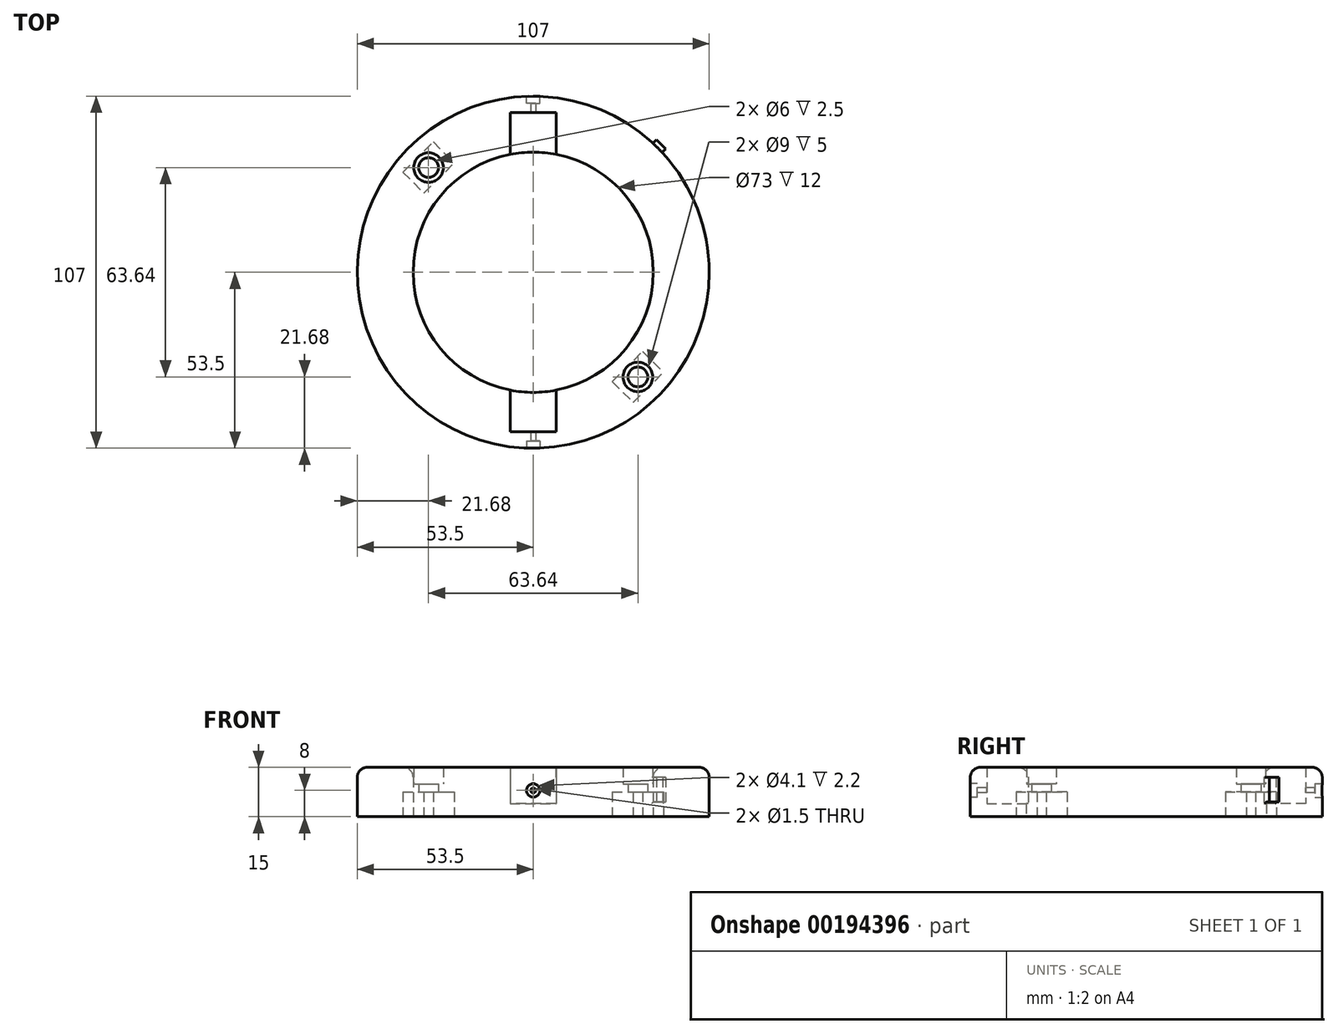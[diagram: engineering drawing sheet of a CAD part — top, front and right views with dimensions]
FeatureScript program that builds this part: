
annotation { "Feature Type Name" : "Feature", "Feature Type Description" : "" }
export const myFeature = defineFeature(function(context is Context, id is Id, definition is map)
    precondition{}
    {
        {
            var Q0;
            Q0=qCreatedBy(makeId("Top.planeOp"),FACE);
            var sketch = newSketch(context, id + "F0", { "sketchPlane" : qUnion([Q0])});
            skCircle(sketch, "E0", {"center": v(0, 0) * mm, "radius": 36.5 * mm});
            skCircle(sketch, "E1", {"center": v(0, 0) * mm, "radius": 53.5 * mm});
            skSolve(sketch);
        }
        {
            var Q0;
            Q0=makeQuery(id+"F0.imprint","IMPRINT",FACE,{"disambiguationData":[TD([[makeQuery(id+"F0.imprint","IMPRINT",EDGE,{"derivedFrom":sQuery(id+"F0.wireOp",EDGE,"E0")}),-1.0]])]});
            extrude(context, id + "F1", {"entities" : qUnion([Q0]), "depth" : 15 * mm});
        }
        {
            var Q0;
            Q0=qCreatedBy(makeId("Top.planeOp"),FACE);
            var sketch = newSketch(context, id + "F2", { "sketchPlane" : qUnion([Q0])});
            skPoint(sketch, "E2", {"position": v(0, 36.5) * mm});
            skPoint(sketch, "E3", {"position": v(0, -33.5) * mm});
            skPoint(sketch, "E4", {"position": v(0, 33.5) * mm});
            skPoint(sketch, "E5", {"position": v(0, 50.5) * mm});
            skPoint(sketch, "E6", {"position": v(0, -36.5) * mm});
            skPoint(sketch, "E7", {"position": v(0, -50.5) * mm});
            skPoint(sketch, "E8", {"position": v(0, 53.5) * mm});
            skPoint(sketch, "E9", {"position": v(0, -53.5) * mm});
            skLineSegment(sketch, "E10", {"start": v(25.8, -25.8) * mm, "end": v(-25.8, 25.8) * mm});
            skLineSegment(sketch, "E11", {"start": v(-25.8, -25.8) * mm, "end": v(25.8, 25.8) * mm});
            skLineSegment(sketch, "E12", {"start": v(-5, 53.5) * mm, "end": v(5, -53.5) * mm});
            skLineSegment(sketch, "E13", {"start": v(0, 53.5) * mm, "end": v(-5, 53.5) * mm});
            skLineSegment(sketch, "E14", {"start": v(0, -53.5) * mm, "end": v(5, -53.5) * mm});
            skSolve(sketch);
        }
        {
            var Q0;
            Q0=sQuery(id+"F2.wireOp",EDGE,"E10");
            cPlane(context, id + "F3", {"entities" : qUnion([Q0]), "cplaneType" : CPlaneType.LINE_ANGLE, "offset" : 25 * mm, "angle" : 90 * degree, "width" : 150 * mm, "height" : 150 * mm});
        }
        {
            var Q0;
            Q0=makeQuery(id+"F1.opExtrude","CAP_FACE",FACE,{"disambiguationData":[OSD([sQuery(id+"F0.wireOp",EDGE,"E0"),sQuery(id+"F0.wireOp",EDGE,"E1")])],"isStart":false});
            var sketch = newSketch(context, id + "F4", { "sketchPlane" : qUnion([Q0])});
            skPoint(sketch, "E15", {"position": v(-31.82, 31.82) * mm});
            skPoint(sketch, "E16", {"position": v(31.82, -31.82) * mm});
            skSolve(sketch);
        }
        {
            var Q0;
            Q0=sQuery(id+"F4.wireOp",VERTEX,"E15");
            var Q1;
            Q1=sQuery(id+"F4.wireOp",VERTEX,"E16");
            var Q2;
            Q2=makeQuery(id+"F1.opExtrude","SWEPT_BODY",BODY,{"disambiguationData":[OSD([sQuery(id+"F0.wireOp",EDGE,"E0"),sQuery(id+"F0.wireOp",EDGE,"E1")])]});
            hole(context, id + "F5", {"style" : HoleStyle.C_BORE, "endStyle" : HoleEndStyle.THROUGH, "holeDiameter" : 6 * mm, "cBoreDiameter" : 9 * mm, "cBoreDepth" : 5 * mm, "locations" : qUnion([Q0, Q1]), "scope" : qUnion([Q2]), "isTappedThrough" : true});
        }
        {
            var Q0;
            Q0=qCreatedBy(makeId("Front.planeOp"),FACE);
            var Q1;
            Q1=sQuery(id+"F2.wireOp",VERTEX,"E4");
            cPlane(context, id + "F6", {"entities" : qUnion([Q0, Q1]), "cplaneType" : CPlaneType.PLANE_POINT, "offset" : 25 * mm, "width" : 150 * mm, "height" : 150 * mm});
        }
        {
            var Q0;
            Q0=qCreatedBy(id+"F6.planeOp",FACE);
            var sketch = newSketch(context, id + "F7", { "sketchPlane" : qUnion([Q0])});
            skLineSegment(sketch, "E17.bottom", {"start": v(-7, 15) * mm, "end": v(7, 15) * mm});
            skLineSegment(sketch, "E17.top", {"start": v(-7, 4) * mm, "end": v(7, 4) * mm});
            skLineSegment(sketch, "E17.left", {"start": v(-7, 15) * mm, "end": v(-7, 4) * mm});
            skLineSegment(sketch, "E17.right", {"start": v(7, 15) * mm, "end": v(7, 4) * mm});
            skSolve(sketch);
        }
        {
            var Q0;
            Q0=makeQuery(id+"F7.imprint","IMPRINT",FACE,{"disambiguationData":[TD([[makeQuery(id+"F7.imprint","IMPRINT",EDGE,{"derivedFrom":sQuery(id+"F7.wireOp",EDGE,"E17.bottom")}),-1.0]])]});
            extrude(context, id + "F8", {"entities" : qUnion([Q0]), "operationType" : NewBodyOperationType.REMOVE, "oppositeDirection" : true, "depth" : 15 * mm});
        }
        {
            var Q0;
            Q0=qCreatedBy(makeId("Front.planeOp"),FACE);
            var Q1;
            Q1=sQuery(id+"F2.wireOp",VERTEX,"E3");
            cPlane(context, id + "F9", {"entities" : qUnion([Q0, Q1]), "cplaneType" : CPlaneType.PLANE_POINT, "offset" : 25 * mm, "width" : 150 * mm, "height" : 150 * mm});
        }
        {
            var Q0;
            Q0=qCreatedBy(id+"F9.planeOp",FACE);
            var sketch = newSketch(context, id + "F10", { "sketchPlane" : qUnion([Q0])});
            skLineSegment(sketch, "E18.bottom", {"start": v(7, 15) * mm, "end": v(-7, 15) * mm});
            skLineSegment(sketch, "E18.top", {"start": v(7, 4) * mm, "end": v(-7, 4) * mm});
            skLineSegment(sketch, "E18.left", {"start": v(7, 15) * mm, "end": v(7, 4) * mm});
            skLineSegment(sketch, "E18.right", {"start": v(-7, 15) * mm, "end": v(-7, 4) * mm});
            skSolve(sketch);
        }
        {
            var Q0;
            Q0=makeQuery(id+"F10.imprint","IMPRINT",FACE,{"disambiguationData":[TD([[makeQuery(id+"F10.imprint","IMPRINT",EDGE,{"derivedFrom":sQuery(id+"F10.wireOp",EDGE,"E18.bottom")}),1.0]])]});
            extrude(context, id + "F11", {"entities" : qUnion([Q0]), "operationType" : NewBodyOperationType.REMOVE, "depth" : 15 * mm});
        }
        {
            var Q0;
            Q0=qCreatedBy(makeId("Front.planeOp"),FACE);
            var Q1;
            Q1=sQuery(id+"F2.wireOp",VERTEX,"E9");
            cPlane(context, id + "F12", {"entities" : qUnion([Q0, Q1]), "cplaneType" : CPlaneType.PLANE_POINT, "offset" : 25 * mm, "width" : 150 * mm, "height" : 150 * mm});
        }
        {
            var Q0;
            Q0=qCreatedBy(id+"F12.planeOp",FACE);
            var sketch = newSketch(context, id + "F13", { "sketchPlane" : qUnion([Q0])});
            skCircle(sketch, "E19", {"center": v(0, 8) * mm, "radius": 2.05 * mm});
            skSolve(sketch);
        }
        {
            var Q0;
            Q0=makeQuery(id+"F13.imprint","IMPRINT",FACE,{"disambiguationData":[TD([[makeQuery(id+"F13.imprint","IMPRINT",EDGE,{"derivedFrom":sQuery(id+"F13.wireOp",EDGE,"E19")}),1.0]])]});
            extrude(context, id + "F14", {"entities" : qUnion([Q0]), "operationType" : NewBodyOperationType.REMOVE, "oppositeDirection" : true, "depth" : 2.2 * mm});
        }
        {
            var Q0;
            Q0=qCreatedBy(makeId("Front.planeOp"),FACE);
            var Q1;
            Q1=sQuery(id+"F2.wireOp",VERTEX,"E8");
            cPlane(context, id + "F15", {"entities" : qUnion([Q0, Q1]), "cplaneType" : CPlaneType.PLANE_POINT, "offset" : 25 * mm, "width" : 150 * mm, "height" : 150 * mm});
        }
        {
            var Q0;
            Q0=qCreatedBy(id+"F15.planeOp",FACE);
            var sketch = newSketch(context, id + "F16", { "sketchPlane" : qUnion([Q0])});
            skCircle(sketch, "E20", {"center": v(0, 8) * mm, "radius": 2.05 * mm});
            skSolve(sketch);
        }
        {
            var Q0;
            Q0=makeQuery(id+"F16.imprint","IMPRINT",FACE,{"disambiguationData":[TD([[makeQuery(id+"F16.imprint","IMPRINT",EDGE,{"derivedFrom":sQuery(id+"F16.wireOp",EDGE,"E20")}),1.0]])]});
            extrude(context, id + "F17", {"entities" : qUnion([Q0]), "operationType" : NewBodyOperationType.REMOVE, "depth" : 2.2 * mm});
        }
        {
            var Q0;
            Q0=makeQuery(id+"F1.opExtrude","CAP_FACE",FACE,{"disambiguationData":[OSD([sQuery(id+"F0.wireOp",EDGE,"E0"),sQuery(id+"F0.wireOp",EDGE,"E1")])],"isStart":true});
            var sketch = newSketch(context, id + "F18", { "sketchPlane" : qUnion([Q0])});
            skLineSegment(sketch, "E21.bottom", {"start": v(-39.6, -30.4) * mm, "end": v(-33.23, -24.04) * mm});
            skLineSegment(sketch, "E21.top", {"start": v(-30.4, -39.6) * mm, "end": v(-24.04, -33.23) * mm});
            skLineSegment(sketch, "E21.left", {"start": v(-39.6, -30.4) * mm, "end": v(-30.4, -39.6) * mm});
            skLineSegment(sketch, "E21.right", {"start": v(-33.23, -24.04) * mm, "end": v(-24.04, -33.23) * mm});
            skLineSegment(sketch, "E22.bottom", {"start": v(24.04, 33.23) * mm, "end": v(30.4, 39.6) * mm});
            skLineSegment(sketch, "E22.top", {"start": v(33.23, 24.04) * mm, "end": v(39.6, 30.4) * mm});
            skLineSegment(sketch, "E22.left", {"start": v(24.04, 33.23) * mm, "end": v(33.23, 24.04) * mm});
            skLineSegment(sketch, "E22.right", {"start": v(30.4, 39.6) * mm, "end": v(39.6, 30.4) * mm});
            skSolve(sketch);
        }
        {
            var Q0;
            Q0=makeQuery(id+"F18.imprint","IMPRINT",FACE,{"disambiguationData":[TD([[makeQuery(id+"F18.imprint","IMPRINT",EDGE,{"derivedFrom":sQuery(id+"F18.wireOp",EDGE,"E21.bottom")}),-1.0]])]});
            extrude(context, id + "F19", {"entities" : qUnion([Q0]), "operationType" : NewBodyOperationType.REMOVE, "oppositeDirection" : true, "depth" : 7.5 * mm});
        }
        {
            var Q0;
            Q0 = qSketchRegion(id + "F18", true);
            extrude(context, id + "F20", {"entities" : qUnion([Q0]), "operationType" : NewBodyOperationType.REMOVE, "oppositeDirection" : true, "depth" : 7.5 * mm});
        }
        {
            var Q0;
            Q0=makeQuery(id+"F1.opExtrude","CAP_EDGE",EDGE,{"disambiguationData":[OSD([sQuery(id+"F0.wireOp",EDGE,"E0")])],"isStart":false});
            fillet(context, id + "F21", {"entities" : qUnion([Q0]), "radius" : 3 * mm, "tangentPropagation" : true, "allowEdgeOverflow" : false});
        }
        {
            var Q0;
            Q0=makeQuery(id+"F1.opExtrude","CAP_EDGE",EDGE,{"disambiguationData":[OSD([sQuery(id+"F0.wireOp",EDGE,"E1")])],"isStart":false});
            fillet(context, id + "F22", {"entities" : qUnion([Q0]), "radius" : 3 * mm, "tangentPropagation" : true, "allowEdgeOverflow" : false});
        }
        {
            var Q0;
            Q0=qCreatedBy(makeId("Top.planeOp"),FACE);
            var sketch = newSketch(context, id + "F23", { "sketchPlane" : qUnion([Q0])});
            skPoint(sketch, "E23", {"position": v(-37.83, 37.83) * mm});
            skPoint(sketch, "E24.1.0", {"position": v(-37.83, -37.83) * mm});
            skPoint(sketch, "E24.2.0", {"position": v(37.83, -37.83) * mm});
            skPoint(sketch, "E24.3.0", {"position": v(37.83, 37.83) * mm});
            skPoint(sketch, "E24.center", {"position": v(0, 0) * mm});
            skLineSegment(sketch, "E25", {"start": v(37.83, 37.83) * mm, "end": v(74.08, 1.58) * mm});
            skLineSegment(sketch, "E26", {"start": v(37.83, -37.83) * mm, "end": v(13.7, -61.95) * mm});
            skLineSegment(sketch, "E27", {"start": v(-37.83, -37.83) * mm, "end": v(-65, -10.65) * mm});
            skLineSegment(sketch, "E28", {"start": v(-37.83, 37.83) * mm, "end": v(-13.77, 61.9) * mm});
            skSolve(sketch);
        }
        {
            var Q0;
            Q0=qCreatedBy(id+"F3.planeOp",FACE);
            var Q1;
            Q1=sQuery(id+"F23.wireOp",VERTEX,"E24.3.0");
            cPlane(context, id + "F24", {"entities" : qUnion([Q0, Q1]), "cplaneType" : CPlaneType.PLANE_POINT, "offset" : 25 * mm, "width" : 150 * mm, "height" : 150 * mm});
        }
        {
            var Q0;
            Q0=qCreatedBy(id+"F24.planeOp",FACE);
            var sketch = newSketch(context, id + "F25", { "sketchPlane" : qUnion([Q0])});
            skLineSegment(sketch, "E29.bottom", {"start": v(-2, 12) * mm, "end": v(2, 12) * mm});
            skLineSegment(sketch, "E29.top", {"start": v(2, 4.5) * mm, "end": v(-2, 4.5) * mm});
            skLineSegment(sketch, "E29.left", {"start": v(2, 12) * mm, "end": v(2, 4.5) * mm});
            skLineSegment(sketch, "E29.right", {"start": v(-2, 12) * mm, "end": v(-2, 4.5) * mm});
            skSolve(sketch);
        }
        {
            var Q0;
            Q0=makeQuery(id+"F25.imprint","IMPRINT",FACE,{"disambiguationData":[TD([[makeQuery(id+"F25.imprint","IMPRINT",EDGE,{"derivedFrom":sQuery(id+"F25.wireOp",EDGE,"E29.bottom")}),1.0]])]});
            var Q1;
            Q1=makeQuery(id+"F25.imprint","IMPRINT",FACE,{"disambiguationData":[TD([[makeQuery(id+"F25.imprint","IMPRINT",EDGE,{"derivedFrom":sQuery(id+"F25.wireOp",EDGE,"E29.bottom")}),-1.0]])]});
            extrude(context, id + "F26", {"entities" : qUnion([Q0, Q1]), "operationType" : NewBodyOperationType.ADD, "oppositeDirection" : true, "depth" : 3 * mm, "symmetric" : true});
        }
        {
            var Q0;
            Q0=makeQuery(id+"F26.boolean.opBoolean","INTERSECT",EDGE,{"derivedFrom":[makeQuery(id+"F1.opExtrude","SWEPT_FACE",FACE,{"disambiguationData":[OSD([sQuery(id+"F0.wireOp",EDGE,"E1")])]}),makeQuery(id+"F26.opExtrude","SWEPT_FACE",FACE,{"disambiguationData":[OSD([sQuery(id+"F25.wireOp",EDGE,"E29.right")])]})]});
            var Q1;
            Q1=makeQuery(id+"F26.boolean.opBoolean","INTERSECT",EDGE,{"derivedFrom":[makeQuery(id+"F1.opExtrude","SWEPT_FACE",FACE,{"disambiguationData":[OSD([sQuery(id+"F0.wireOp",EDGE,"E1")])]}),makeQuery(id+"F26.opExtrude","SWEPT_FACE",FACE,{"disambiguationData":[OSD([sQuery(id+"F25.wireOp",EDGE,"E29.left")])]})]});
            var Q2;
            Q2=makeQuery(id+"F26.boolean.opBoolean","INTERSECT",EDGE,{"derivedFrom":[makeQuery(id+"F1.opExtrude","SWEPT_FACE",FACE,{"disambiguationData":[OSD([sQuery(id+"F0.wireOp",EDGE,"E1")])]}),makeQuery(id+"F26.opExtrude","SWEPT_FACE",FACE,{"disambiguationData":[OSD([sQuery(id+"F25.wireOp",EDGE,"E29.top")])]})]});
            var Q3;
            Q3=makeQuery(id+"F26.opExtrude","CAP_EDGE",EDGE,{"disambiguationData":[OSD([sQuery(id+"F25.wireOp",EDGE,"E29.right")])],"isStart":false});
            var Q4;
            Q4=makeQuery(id+"F26.opExtrude","CAP_EDGE",EDGE,{"disambiguationData":[OSD([sQuery(id+"F25.wireOp",EDGE,"E29.top")])],"isStart":false});
            var Q5;
            Q5=makeQuery(id+"F26.opExtrude","CAP_EDGE",EDGE,{"disambiguationData":[OSD([sQuery(id+"F25.wireOp",EDGE,"E29.left")])],"isStart":false});
            var Q6;
            Q6=makeQuery(id+"F26.opExtrude","CAP_EDGE",EDGE,{"disambiguationData":[OSD([sQuery(id+"F25.wireOp",EDGE,"E29.bottom")])],"isStart":false});
            fillet(context, id + "F27", {"entities" : qUnion([Q0, Q1, Q2, Q3, Q4, Q5, Q6]), "radius" : 0.5 * mm, "tangentPropagation" : true, "allowEdgeOverflow" : false});
        }
        {
            var Q0;
            Q0=makeQuery(id+"F17.boolean.opBoolean","COPY",FACE,{"derivedFrom":makeQuery(id+"F17.opExtrude","CAP_FACE",FACE,{"disambiguationData":[OSD([sQuery(id+"F16.wireOp",EDGE,"E20")])],"isStart":false})});
            var sketch = newSketch(context, id + "F28", { "sketchPlane" : qUnion([Q0])});
            skPoint(sketch, "E30", {"position": v(0, 8) * mm});
            skSolve(sketch);
        }
        {
            var Q0;
            Q0=sQuery(id+"F28.wireOp",VERTEX,"E30");
            var Q1;
            Q1=makeQuery(id+"F1.opExtrude","SWEPT_BODY",BODY,{"disambiguationData":[OSD([sQuery(id+"F0.wireOp",EDGE,"E0"),sQuery(id+"F0.wireOp",EDGE,"E1")])]});
            hole(context, id + "F29", {"style" : HoleStyle.SIMPLE, "endStyle" : HoleEndStyle.THROUGH, "holeDiameter" : 1.5 * mm, "locations" : qUnion([Q0]), "scope" : qUnion([Q1]), "isTappedThrough" : true});
        }
    });
